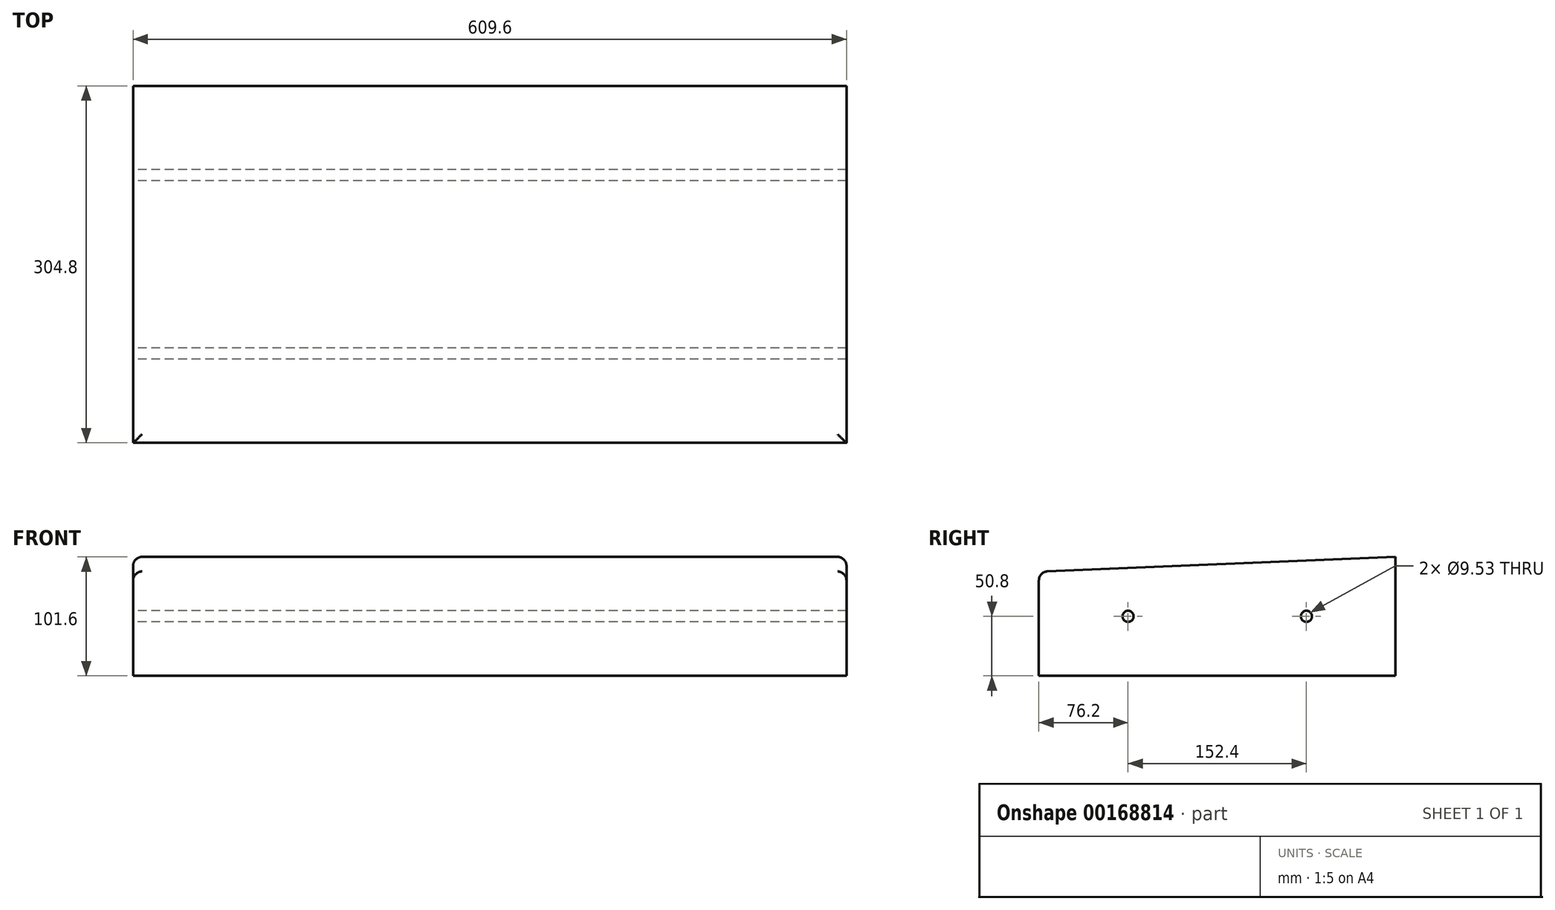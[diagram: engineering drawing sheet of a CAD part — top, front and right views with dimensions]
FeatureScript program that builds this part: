
annotation { "Feature Type Name" : "Feature", "Feature Type Description" : "" }
export const myFeature = defineFeature(function(context is Context, id is Id, definition is map)
    precondition{}
    {
        {
            var Q0;
            Q0=qCreatedBy(makeId("Right.planeOp"),FACE);
            var sketch = newSketch(context, id + "F0", { "sketchPlane" : qUnion([Q0])});
            skLineSegment(sketch, "E0", {"start": v(0, 0) * mm, "end": v(-304.8, 0) * mm});
            skLineSegment(sketch, "E1", {"start": v(0, 0) * mm, "end": v(0, 101.6) * mm});
            skLineSegment(sketch, "E2", {"start": v(0, 101.6) * mm, "end": v(-304.8, 88.9) * mm});
            skLineSegment(sketch, "E3", {"start": v(-304.8, 88.9) * mm, "end": v(-304.8, 0) * mm});
            skCircle(sketch, "E4", {"center": v(-76.2, 50.8) * mm, "radius": 4.76 * mm});
            skPoint(sketch, "E5", {"position": v(-152.4, 0) * mm});
            skLineSegment(sketch, "E6", {"start": v(-152.4, 0) * mm, "end": v(-152.4, 102.89) * mm, "construction": true});
            skCircle(sketch, "E7.MirrorC", {"center": v(-228.6, 50.8) * mm, "radius": 4.76 * mm});
            skSolve(sketch);
        }
        {
            var Q0;
            Q0 = qSketchRegion(id + "F0", true);
            extrude(context, id + "F1", {"entities" : qUnion([Q0]), "endBound" : BoundingType.SYMMETRIC, "depth" : 609.6 * mm});
        }
        {
            var Q0;
            Q0=makeQuery(id+"F1.opExtrude","SWEPT_EDGE",EDGE,{"disambiguationData":[OSD([sQuery(id+"F0.wireOp",EDGE,"E2"),sQuery(id+"F0.wireOp",EDGE,"E3")])]});
            var Q1;
            Q1=makeQuery(id+"F1.opExtrude","CAP_EDGE",EDGE,{"disambiguationData":[OSD([sQuery(id+"F0.wireOp",EDGE,"E2")])],"isStart":true});
            var Q2;
            Q2=makeQuery(id+"F1.opExtrude","CAP_EDGE",EDGE,{"disambiguationData":[OSD([sQuery(id+"F0.wireOp",EDGE,"E2")])],"isStart":false});
            fillet(context, id + "F2", {"entities" : qUnion([Q0, Q1, Q2]), "radius" : 7.62 * mm, "tangentPropagation" : true, "allowEdgeOverflow" : false});
        }
    });
